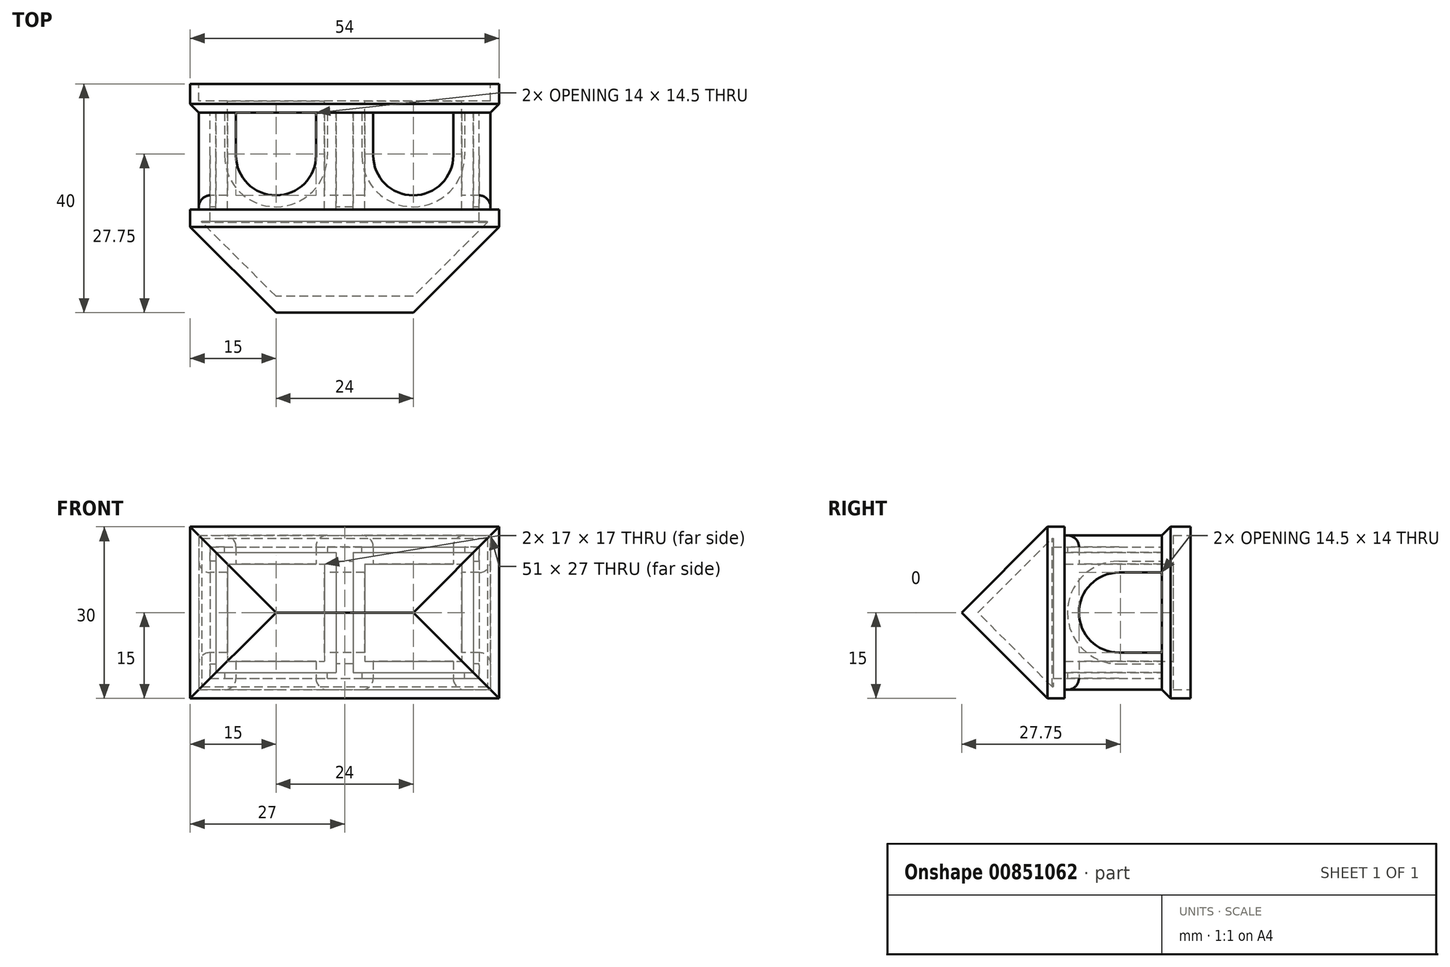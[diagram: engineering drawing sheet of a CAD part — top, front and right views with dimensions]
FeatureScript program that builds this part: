
annotation { "Feature Type Name" : "Feature", "Feature Type Description" : "" }
export const myFeature = defineFeature(function(context is Context, id is Id, definition is map)
    precondition{}
    {
        {
            var Q0;
            Q0=qCreatedBy(makeId("Front.planeOp"),FACE);
            var sketch = newSketch(context, id + "F0", { "sketchPlane" : qUnion([Q0])});
            skLineSegment(sketch, "E0.bottom", {"start": v(0, 0) * mm, "end": v(54, 0) * mm});
            skLineSegment(sketch, "E0.top", {"start": v(0, 30) * mm, "end": v(54, 30) * mm});
            skLineSegment(sketch, "E0.left", {"start": v(0, 0) * mm, "end": v(0, 30) * mm});
            skLineSegment(sketch, "E0.right", {"start": v(54, 0) * mm, "end": v(54, 30) * mm});
            skLineSegment(sketch, "E1.bottom", {"start": v(1.5, 28.5) * mm, "end": v(52.5, 28.5) * mm});
            skLineSegment(sketch, "E1.top", {"start": v(1.5, 1.5) * mm, "end": v(52.5, 1.5) * mm});
            skLineSegment(sketch, "E1.left", {"start": v(1.5, 28.5) * mm, "end": v(1.5, 1.5) * mm});
            skLineSegment(sketch, "E1.right", {"start": v(52.5, 28.5) * mm, "end": v(52.5, 1.5) * mm});
            skLineSegment(sketch, "E2.bottom", {"start": v(6.5, 23.5) * mm, "end": v(23.5, 23.5) * mm});
            skLineSegment(sketch, "E2.top", {"start": v(6.5, 6.5) * mm, "end": v(23.5, 6.5) * mm});
            skLineSegment(sketch, "E2.left", {"start": v(6.5, 23.5) * mm, "end": v(6.5, 6.5) * mm});
            skLineSegment(sketch, "E2.right", {"start": v(23.5, 23.5) * mm, "end": v(23.5, 6.5) * mm});
            skLineSegment(sketch, "E3.bottom", {"start": v(30.5, 23.5) * mm, "end": v(47.5, 23.5) * mm});
            skLineSegment(sketch, "E3.top", {"start": v(30.5, 6.5) * mm, "end": v(47.5, 6.5) * mm});
            skLineSegment(sketch, "E3.left", {"start": v(30.5, 23.5) * mm, "end": v(30.5, 6.5) * mm});
            skLineSegment(sketch, "E3.right", {"start": v(47.5, 23.5) * mm, "end": v(47.5, 6.5) * mm});
            skPoint(sketch, "E4", {"position": v(6.5, 28.5) * mm});
            skPoint(sketch, "E5", {"position": v(23.5, 23.5) * mm});
            skPoint(sketch, "E6", {"position": v(30.5, 23.5) * mm});
            skPoint(sketch, "E7", {"position": v(30.5, 28.5) * mm});
            skPoint(sketch, "E8", {"position": v(47.5, 23.5) * mm});
            skPoint(sketch, "E9", {"position": v(52.5, 23.5) * mm});
            skLineSegment(sketch, "E10", {"start": v(52.5, 23.5) * mm, "end": v(1.5, 23.5) * mm});
            skLineSegment(sketch, "E11", {"start": v(1.5, 6.5) * mm, "end": v(52.5, 6.5) * mm});
            skLineSegment(sketch, "E12", {"start": v(23.5, 28.5) * mm, "end": v(23.5, 1.5) * mm});
            skLineSegment(sketch, "E13", {"start": v(30.5, 28.5) * mm, "end": v(30.5, 1.5) * mm});
            skLineSegment(sketch, "E14", {"start": v(47.5, 6.5) * mm, "end": v(47.5, 1.5) * mm});
            skLineSegment(sketch, "E15", {"start": v(6.5, 6.5) * mm, "end": v(6.5, 1.5) * mm});
            skLineSegment(sketch, "E16", {"start": v(6.5, 23.5) * mm, "end": v(6.5, 28.5) * mm});
            skLineSegment(sketch, "E17", {"start": v(47.5, 23.5) * mm, "end": v(47.5, 28.5) * mm});
            skSolve(sketch);
        }
        {
            var Q0;
            {var subQ0=sQuery(id+"F0.wireOp",EDGE,"E16");Q0=makeQuery(id+"F0.imprint","IMPRINT",FACE,{"disambiguationData":[TD([[makeQuery(id+"F0.imprint","IMPRINT",EDGE,{"derivedFrom":subQ0}),1.0]])]});}
            var Q1;
            {var subQ0=sQuery(id+"F0.wireOp",EDGE,"E13");var subQ1=sQuery(id+"F0.wireOp",EDGE,"E1.bottom");var subQ2=makeQuery(id+"F0.imprint","INTERSECT",VERTEX,{"derivedFrom":[subQ1,subQ0]});Q1=makeQuery(id+"F0.imprint","IMPRINT",FACE,{"disambiguationData":[TD([[makeQuery(id+"F0.imprint","IMPRINT",EDGE,{"disambiguationData":[TD([[subQ2,1.0]])],"derivedFrom":subQ1}),-1.0]])]});}
            var Q2;
            {var subQ3=sQuery(id+"F0.wireOp",EDGE,"E17");Q2=makeQuery(id+"F0.imprint","IMPRINT",FACE,{"disambiguationData":[TD([[makeQuery(id+"F0.imprint","IMPRINT",EDGE,{"derivedFrom":subQ3}),-1.0]])]});}
            var Q3;
            {var subQ3=sQuery(id+"F0.wireOp",EDGE,"E14");Q3=makeQuery(id+"F0.imprint","IMPRINT",FACE,{"disambiguationData":[TD([[makeQuery(id+"F0.imprint","IMPRINT",EDGE,{"derivedFrom":subQ3}),1.0]])]});}
            var Q4;
            {var subQ0=sQuery(id+"F0.wireOp",EDGE,"E13");var subQ1=sQuery(id+"F0.wireOp",EDGE,"E1.top");var subQ2=makeQuery(id+"F0.imprint","INTERSECT",VERTEX,{"derivedFrom":[subQ1,subQ0]});Q4=makeQuery(id+"F0.imprint","IMPRINT",FACE,{"disambiguationData":[TD([[makeQuery(id+"F0.imprint","IMPRINT",EDGE,{"disambiguationData":[TD([[subQ2,1.0]])],"derivedFrom":subQ1}),1.0]])]});}
            var Q5;
            {var subQ0=sQuery(id+"F0.wireOp",EDGE,"E15");Q5=makeQuery(id+"F0.imprint","IMPRINT",FACE,{"disambiguationData":[TD([[makeQuery(id+"F0.imprint","IMPRINT",EDGE,{"derivedFrom":subQ0}),-1.0]])]});}
            var Q6;
            {var subQ4=sQuery(id+"F0.wireOp",EDGE,"E2.top");Q6=makeQuery(id+"F0.imprint","IMPRINT",FACE,{"disambiguationData":[TD([[makeQuery(id+"F0.imprint","IMPRINT",EDGE,{"derivedFrom":subQ4}),-1.0]])]});}
            var Q7;
            {var subQ4=sQuery(id+"F0.wireOp",EDGE,"E3.top");Q7=makeQuery(id+"F0.imprint","IMPRINT",FACE,{"disambiguationData":[TD([[makeQuery(id+"F0.imprint","IMPRINT",EDGE,{"derivedFrom":subQ4}),-1.0]])]});}
            var Q8;
            {var subQ5=sQuery(id+"F0.wireOp",EDGE,"E3.right");Q8=makeQuery(id+"F0.imprint","IMPRINT",FACE,{"disambiguationData":[TD([[makeQuery(id+"F0.imprint","IMPRINT",EDGE,{"derivedFrom":subQ5}),1.0]])]});}
            var Q9;
            {var subQ4=sQuery(id+"F0.wireOp",EDGE,"E3.bottom");Q9=makeQuery(id+"F0.imprint","IMPRINT",FACE,{"disambiguationData":[TD([[makeQuery(id+"F0.imprint","IMPRINT",EDGE,{"derivedFrom":subQ4}),1.0]])]});}
            var Q10;
            {var subQ4=sQuery(id+"F0.wireOp",EDGE,"E2.bottom");Q10=makeQuery(id+"F0.imprint","IMPRINT",FACE,{"disambiguationData":[TD([[makeQuery(id+"F0.imprint","IMPRINT",EDGE,{"derivedFrom":subQ4}),1.0]])]});}
            var Q11;
            {var subQ5=sQuery(id+"F0.wireOp",EDGE,"E2.left");Q11=makeQuery(id+"F0.imprint","IMPRINT",FACE,{"disambiguationData":[TD([[makeQuery(id+"F0.imprint","IMPRINT",EDGE,{"derivedFrom":subQ5}),-1.0]])]});}
            var Q12;
            {var subQ0=sQuery(id+"F0.wireOp",EDGE,"E2.right");Q12=makeQuery(id+"F0.imprint","IMPRINT",FACE,{"disambiguationData":[TD([[makeQuery(id+"F0.imprint","IMPRINT",EDGE,{"derivedFrom":subQ0}),1.0]])]});}
            extrude(context, id + "F1", {"entities" : qUnion([Q0, Q1, Q2, Q3, Q4, Q5, Q6, Q7, Q8, Q9, Q10, Q11, Q12]), "depth" : 22 * mm, "offsetDistance" : 25 * mm});
        }
        {
            var Q0;
            Q0=makeQuery(id+"F0.imprint","IMPRINT",FACE,{"disambiguationData":[TD([[makeQuery(id+"F0.imprint","IMPRINT",EDGE,{"derivedFrom":sQuery(id+"F0.wireOp",EDGE,"E0.bottom")}),1.0]])]});
            extrude(context, id + "F2", {"entities" : qUnion([Q0]), "operationType" : NewBodyOperationType.ADD, "depth" : 5 * mm, "offsetDistance" : 25 * mm});
        }
        {
            var Q0;
            Q0=qCreatedBy(makeId("Top.planeOp"),FACE);
            var sketch = newSketch(context, id + "F3", { "sketchPlane" : qUnion([Q0])});
            skPoint(sketch, "E18", {"position": v(1.5, -12.5) * mm});
            skPoint(sketch, "E19", {"position": v(6.5, -12.5) * mm});
            skLineSegment(sketch, "E20", {"start": v(1.5, -12.5) * mm, "end": v(52.5, -12.5) * mm});
            skPoint(sketch, "E21", {"position": v(47.5, -12.5) * mm});
            skPoint(sketch, "E22", {"position": v(23.5, -12.5) * mm});
            skPoint(sketch, "E23", {"position": v(30.5, -12.5) * mm});
            skPoint(sketch, "E24", {"position": v(15, -12.5) * mm});
            skPoint(sketch, "E25", {"position": v(39, -12.5) * mm});
            skArc(sketch, "E26", {"start": v(8, -12.5) * mm, "mid": v(15, -19.5) * mm, "end": v(22, -12.5) * mm});
            skArc(sketch, "E27", {"start": v(32, -12.5) * mm, "mid": v(39, -19.5) * mm, "end": v(46, -12.5) * mm});
            skLineSegment(sketch, "E28.bottom", {"start": v(8, -12.5) * mm, "end": v(22, -12.5) * mm});
            skLineSegment(sketch, "E28.top", {"start": v(8, -5) * mm, "end": v(22, -5) * mm});
            skLineSegment(sketch, "E28.left", {"start": v(8, -12.5) * mm, "end": v(8, -5) * mm});
            skLineSegment(sketch, "E28.right", {"start": v(22, -12.5) * mm, "end": v(22, -5) * mm});
            skLineSegment(sketch, "E29.bottom", {"start": v(32, -12.5) * mm, "end": v(46, -12.5) * mm});
            skLineSegment(sketch, "E29.top", {"start": v(32, -5) * mm, "end": v(46, -5) * mm});
            skLineSegment(sketch, "E29.left", {"start": v(32, -12.5) * mm, "end": v(32, -5) * mm});
            skLineSegment(sketch, "E29.right", {"start": v(46, -12.5) * mm, "end": v(46, -5) * mm});
            skSolve(sketch);
        }
        {
            var Q0;
            {var subQ0=sQuery(id+"F3.wireOp",EDGE,"E26");Q0=makeQuery(id+"F3.imprint","IMPRINT",FACE,{"disambiguationData":[TD([[makeQuery(id+"F3.imprint","IMPRINT",EDGE,{"derivedFrom":subQ0}),1.0]])]});}
            var Q1;
            {var subQ0=sQuery(id+"F3.wireOp",EDGE,"E27");Q1=makeQuery(id+"F3.imprint","IMPRINT",FACE,{"disambiguationData":[TD([[makeQuery(id+"F3.imprint","IMPRINT",EDGE,{"derivedFrom":subQ0}),1.0]])]});}
            var Q2;
            Q2=makeQuery(id+"F3.imprint","IMPRINT",FACE,{"disambiguationData":[TD([[makeQuery(id+"F3.imprint","IMPRINT",EDGE,{"derivedFrom":sQuery(id+"F3.wireOp",EDGE,"E29.top")}),-1.0]])]});
            var Q3;
            Q3=makeQuery(id+"F3.imprint","IMPRINT",FACE,{"disambiguationData":[TD([[makeQuery(id+"F3.imprint","IMPRINT",EDGE,{"derivedFrom":sQuery(id+"F3.wireOp",EDGE,"E28.top")}),-1.0]])]});
            extrude(context, id + "F4", {"entities" : qUnion([Q0, Q1, Q2, Q3]), "operationType" : NewBodyOperationType.REMOVE, "depth" : 35 * mm, "offsetDistance" : 25 * mm});
        }
        {
            var Q0;
            Q0=qCreatedBy(makeId("Right.planeOp"),FACE);
            var sketch = newSketch(context, id + "F5", { "sketchPlane" : qUnion([Q0])});
            skPoint(sketch, "E30", {"position": v(-12.5, 22) * mm});
            skPoint(sketch, "E31", {"position": v(-12.5, 8) * mm});
            skLineSegment(sketch, "E32.bottom", {"start": v(-12.5, 22) * mm, "end": v(-5, 22) * mm});
            skLineSegment(sketch, "E32.top", {"start": v(-12.5, 8) * mm, "end": v(-5, 8) * mm});
            skLineSegment(sketch, "E32.left", {"start": v(-12.5, 22) * mm, "end": v(-12.5, 8) * mm});
            skLineSegment(sketch, "E32.right", {"start": v(-5, 22) * mm, "end": v(-5, 8) * mm});
            skPoint(sketch, "E33", {"position": v(-12.5, 15) * mm});
            skArc(sketch, "E34", {"start": v(-12.5, 22) * mm, "mid": v(-19.5, 15) * mm, "end": v(-12.5, 8) * mm});
            skSolve(sketch);
        }
        {
            var Q0;
            Q0=makeQuery(id+"F5.imprint","IMPRINT",FACE,{"disambiguationData":[TD([[makeQuery(id+"F5.imprint","IMPRINT",EDGE,{"derivedFrom":sQuery(id+"F5.wireOp",EDGE,"E32.left")}),-1.0]])]});
            var Q1;
            Q1=makeQuery(id+"F5.imprint","IMPRINT",FACE,{"disambiguationData":[TD([[makeQuery(id+"F5.imprint","IMPRINT",EDGE,{"derivedFrom":sQuery(id+"F5.wireOp",EDGE,"E32.bottom")}),-1.0]])]});
            extrude(context, id + "F6", {"entities" : qUnion([Q0, Q1]), "operationType" : NewBodyOperationType.REMOVE, "depth" : 60 * mm, "offsetDistance" : 25 * mm});
        }
        {
            var Q0;
            Q0=makeQuery(id+"F4.boolean.opBoolean","INTERSECT",EDGE,{"derivedFrom":[makeQuery(id+"F1.opExtrude","SWEPT_FACE",FACE,{"disambiguationData":[OSD([sQuery(id+"F0.wireOp",EDGE,"E1.top")])]}),makeQuery(id+"F4.opExtrude","SWEPT_FACE",FACE,{"disambiguationData":[OSD([sQuery(id+"F3.wireOp",EDGE,"E26")])]})]});
            var Q1;
            Q1=makeQuery(id+"F4.boolean.opBoolean","INTERSECT",EDGE,{"derivedFrom":[makeQuery(id+"F1.opExtrude","SWEPT_FACE",FACE,{"disambiguationData":[OSD([sQuery(id+"F0.wireOp",EDGE,"E1.top")])]}),makeQuery(id+"F4.opExtrude","SWEPT_FACE",FACE,{"disambiguationData":[OSD([sQuery(id+"F3.wireOp",EDGE,"E29.left")])]})]});
            var Q2;
            Q2=makeQuery(id+"F6.boolean.opBoolean","INTERSECT",EDGE,{"derivedFrom":[makeQuery(id+"F1.opExtrude","SWEPT_FACE",FACE,{"disambiguationData":[OSD([sQuery(id+"F0.wireOp",EDGE,"E1.left")])]}),makeQuery(id+"F6.opExtrude","SWEPT_FACE",FACE,{"disambiguationData":[OSD([sQuery(id+"F5.wireOp",EDGE,"E32.top")])]})]});
            var Q3;
            Q3=makeQuery(id+"F6.boolean.opBoolean","INTERSECT",EDGE,{"derivedFrom":[makeQuery(id+"F1.opExtrude","SWEPT_FACE",FACE,{"disambiguationData":[OSD([sQuery(id+"F0.wireOp",EDGE,"E1.right")])]}),makeQuery(id+"F6.opExtrude","SWEPT_FACE",FACE,{"disambiguationData":[OSD([sQuery(id+"F5.wireOp",EDGE,"E34")])]})]});
            var Q4;
            Q4=makeQuery(id+"F4.boolean.opBoolean","INTERSECT",EDGE,{"derivedFrom":[makeQuery(id+"F1.opExtrude","SWEPT_FACE",FACE,{"disambiguationData":[OSD([sQuery(id+"F0.wireOp",EDGE,"E1.bottom")])]}),makeQuery(id+"F4.opExtrude","SWEPT_FACE",FACE,{"disambiguationData":[OSD([sQuery(id+"F3.wireOp",EDGE,"E26")])]})]});
            var Q5;
            Q5=makeQuery(id+"F4.boolean.opBoolean","INTERSECT",EDGE,{"derivedFrom":[makeQuery(id+"F1.opExtrude","SWEPT_FACE",FACE,{"disambiguationData":[OSD([sQuery(id+"F0.wireOp",EDGE,"E1.bottom")])]}),makeQuery(id+"F4.opExtrude","SWEPT_FACE",FACE,{"disambiguationData":[OSD([sQuery(id+"F3.wireOp",EDGE,"E29.left")])]})]});
            fillet(context, id + "F7", {"entities" : qUnion([Q0, Q1, Q2, Q3, Q4, Q5]), "radius" : 2 * mm, "tangentPropagation" : true, "allowEdgeOverflow" : false});
        }
        {
            var Q0;
            Q0=qCreatedBy(makeId("Front.planeOp"),FACE);
            var sketch = newSketch(context, id + "F8", { "sketchPlane" : qUnion([Q0])});
            skLineSegment(sketch, "E35.bottom", {"start": v(52.5, 28.5) * mm, "end": v(1.5, 28.5) * mm});
            skLineSegment(sketch, "E35.top", {"start": v(52.5, 1.5) * mm, "end": v(1.5, 1.5) * mm});
            skLineSegment(sketch, "E35.left", {"start": v(52.5, 28.5) * mm, "end": v(52.5, 1.5) * mm});
            skLineSegment(sketch, "E35.right", {"start": v(1.5, 28.5) * mm, "end": v(1.5, 1.5) * mm});
            skSolve(sketch);
        }
        {
            var Q0;
            Q0=makeQuery(id+"F8.imprint","IMPRINT",FACE,{"disambiguationData":[TD([[makeQuery(id+"F8.imprint","IMPRINT",EDGE,{"derivedFrom":sQuery(id+"F8.wireOp",EDGE,"E35.bottom")}),1.0]])]});
            extrude(context, id + "F9", {"entities" : qUnion([Q0]), "operationType" : NewBodyOperationType.REMOVE, "depth" : 3 * mm, "offsetDistance" : 25 * mm});
        }
        {
            var Q0;
            Q0=makeQuery(id+"F2.opExtrude","CAP_EDGE",EDGE,{"disambiguationData":[OSD([sQuery(id+"F0.wireOp",EDGE,"E0.bottom")])],"isStart":false});
            var Q1;
            Q1=makeQuery(id+"F2.opExtrude","CAP_EDGE",EDGE,{"disambiguationData":[OSD([sQuery(id+"F0.wireOp",EDGE,"E0.right")])],"isStart":false});
            var Q2;
            Q2=makeQuery(id+"F4.boolean.opBoolean","INTERSECT",EDGE,{"derivedFrom":[makeQuery(id+"F4.opExtrude","SWEPT_FACE",FACE,{"disambiguationData":[OSD([sQuery(id+"F3.wireOp",EDGE,"E28.top")])]}),makeQuery(id+"F4.opExtrude","SWEPT_FACE",FACE,{"disambiguationData":[OSD([sQuery(id+"F3.wireOp",EDGE,"E29.top")])]})]});
            var Q3;
            Q3=makeQuery(id+"F2.opExtrude","CAP_EDGE",EDGE,{"disambiguationData":[OSD([sQuery(id+"F0.wireOp",EDGE,"E0.left")])],"isStart":false});
            chamfer(context, id + "F10", {"entities" : qUnion([Q0, Q1, Q2, Q3]), "width" : 1.5 * mm, "tangentPropagation" : true});
        }
        {
            var Q0;
            Q0=qCreatedBy(makeId("Top.planeOp"),FACE);
            var sketch = newSketch(context, id + "F11", { "sketchPlane" : qUnion([Q0])});
            skLineSegment(sketch, "E36.bottom", {"start": v(0, -25) * mm, "end": v(54, -25) * mm});
            skLineSegment(sketch, "E36.top", {"start": v(0, -22) * mm, "end": v(54, -22) * mm});
            skLineSegment(sketch, "E36.left", {"start": v(0, -25) * mm, "end": v(0, -22) * mm});
            skLineSegment(sketch, "E36.right", {"start": v(54, -25) * mm, "end": v(54, -22) * mm});
            skSolve(sketch);
        }
        {
            var Q0;
            Q0=makeQuery(id+"F11.imprint","IMPRINT",FACE,{"disambiguationData":[TD([[makeQuery(id+"F11.imprint","IMPRINT",EDGE,{"derivedFrom":sQuery(id+"F11.wireOp",EDGE,"E36.bottom")}),1.0]])]});
            extrude(context, id + "F12", {"entities" : qUnion([Q0]), "operationType" : NewBodyOperationType.ADD, "depth" : 30 * mm, "offsetDistance" : 25 * mm});
        }
        {
            var Q0;
            Q0=makeQuery(id+"F12.opExtrude","SWEPT_FACE",FACE,{"disambiguationData":[OSD([sQuery(id+"F11.wireOp",EDGE,"E36.bottom")])]});
            extrude(context, id + "F13", {"entities" : qUnion([Q0]), "operationType" : NewBodyOperationType.ADD, "depth" : 25 * mm, "offsetDistance" : 25 * mm, "hasDraft" : true, "draftAngle" : 45 * degree, "draftPullDirection" : true});
        }
        {
            var Q0;
            Q0=makeQuery(id+"F12.boolean.opBoolean","SPLIT",FACE,{"disambiguationData":[TD([makeQuery(id+"F1.opExtrude","SWEPT_FACE",FACE,{"disambiguationData":[OSD([sQuery(id+"F0.wireOp",EDGE,"E3.bottom")])]})])],"derivedFrom":makeQuery(id+"F12.opExtrude","SWEPT_FACE",FACE,{"disambiguationData":[OSD([sQuery(id+"F11.wireOp",EDGE,"E36.top")])]})});
            var Q1;
            Q1=makeQuery(id+"F12.boolean.opBoolean","SPLIT",FACE,{"disambiguationData":[TD([makeQuery(id+"F1.opExtrude","SWEPT_FACE",FACE,{"disambiguationData":[OSD([sQuery(id+"F0.wireOp",EDGE,"E2.bottom")])]})])],"derivedFrom":makeQuery(id+"F12.opExtrude","SWEPT_FACE",FACE,{"disambiguationData":[OSD([sQuery(id+"F11.wireOp",EDGE,"E36.top")])]})});
            shell(context, id + "F14", {"entities" : qUnion([Q0, Q1]), "thickness" : 2 * mm});
        }
    });
